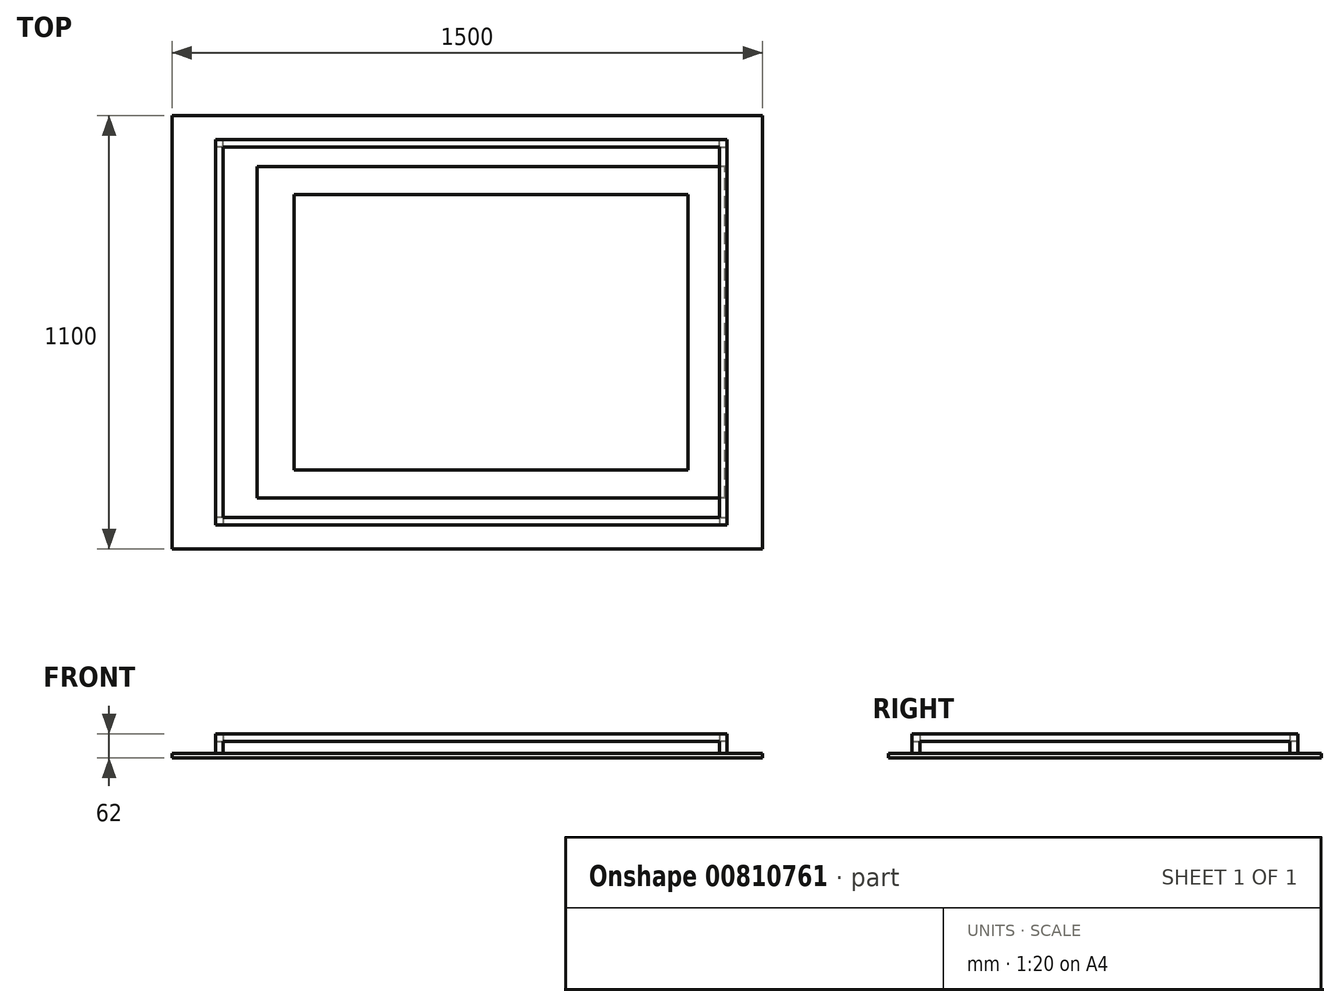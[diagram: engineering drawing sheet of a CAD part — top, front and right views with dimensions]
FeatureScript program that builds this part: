
annotation { "Feature Type Name" : "Feature", "Feature Type Description" : "" }
export const myFeature = defineFeature(function(context is Context, id is Id, definition is map)
    precondition{}
    {
        {
            assignVariable(context, id + "F0", {"name" : "frame_offset", "anyValue" : 40});
        }
        {
            var Q0;
            Q0=qCreatedBy(makeId("Top.planeOp"),FACE);
            var sketch = newSketch(context, id + "F1", { "sketchPlane" : qUnion([Q0])});
            skPoint(sketch, "E0.middle", {"position": v(0, 0) * mm});
            skLineSegment(sketch, "E1.bottom", {"start": v(-640, 480) * mm, "end": v(640, 480) * mm, "construction": true});
            skLineSegment(sketch, "E1.top", {"start": v(-640, -480) * mm, "end": v(640, -480) * mm, "construction": true});
            skLineSegment(sketch, "E1.left", {"start": v(-640, 480) * mm, "end": v(-640, -480) * mm, "construction": true});
            skLineSegment(sketch, "E1.right", {"start": v(640, 480) * mm, "end": v(640, -480) * mm, "construction": true});
            skLineSegment(sketch, "E2.bottom", {"start": v(740, 550) * mm, "end": v(-760, 550) * mm});
            skLineSegment(sketch, "E2.top", {"start": v(740, -550) * mm, "end": v(-760, -550) * mm});
            skLineSegment(sketch, "E2.left", {"start": v(740, 550) * mm, "end": v(740, -550) * mm});
            skLineSegment(sketch, "E2.right", {"start": v(-760, 550) * mm, "end": v(-760, -550) * mm});
            skPoint(sketch, "E2.middle", {"position": v(-10, 0) * mm});
            skLineSegment(sketch, "E3.bottom", {"start": v(-485, 360) * mm, "end": v(585, 360) * mm, "construction": true});
            skLineSegment(sketch, "E3.top", {"start": v(-485, -360) * mm, "end": v(585, -360) * mm, "construction": true});
            skLineSegment(sketch, "E3.left", {"start": v(-485, 360) * mm, "end": v(-485, -360) * mm, "construction": true});
            skLineSegment(sketch, "E3.right", {"start": v(585, 360) * mm, "end": v(585, -360) * mm, "construction": true});
            skPoint(sketch, "E3.middle", {"position": v(50, 0) * mm});
            skSolve(sketch);
        }
        {
            var Q0;
            Q0=qCreatedBy(makeId("Top.planeOp"),FACE);
            var sketch = newSketch(context, id + "F2", { "sketchPlane" : qUnion([Q0])});
            skLineSegment(sketch, "E4.bottom", {"start": v(400, 250) * mm, "end": v(-300, 250) * mm, "construction": true});
            skLineSegment(sketch, "E4.top", {"start": v(400, -250) * mm, "end": v(-300, -250) * mm, "construction": true});
            skLineSegment(sketch, "E4.left", {"start": v(400, 250) * mm, "end": v(400, -250) * mm, "construction": true});
            skLineSegment(sketch, "E4.right", {"start": v(-300, 250) * mm, "end": v(-300, -250) * mm, "construction": true});
            skPoint(sketch, "E4.middle", {"position": v(50, 0) * mm});
            skLineSegment(sketch, "E5.bottom", {"start": v(644.5, -420.5) * mm, "end": v(-544.5, -420.5) * mm, "construction": true});
            skLineSegment(sketch, "E5.top", {"start": v(644.5, 420.5) * mm, "end": v(-544.5, 420.5) * mm, "construction": true});
            skLineSegment(sketch, "E5.left", {"start": v(644.5, -420.5) * mm, "end": v(644.5, 420.5) * mm, "construction": true});
            skLineSegment(sketch, "E5.right", {"start": v(-544.5, -420.5) * mm, "end": v(-544.5, 420.5) * mm, "construction": true});
            skLineSegment(sketch, "E6.bottom", {"start": v(550, 350) * mm, "end": v(-450, 350) * mm, "construction": true});
            skLineSegment(sketch, "E6.top", {"start": v(550, -350) * mm, "end": v(-450, -350) * mm, "construction": true});
            skLineSegment(sketch, "E6.left", {"start": v(550, 350) * mm, "end": v(550, -350) * mm, "construction": true});
            skLineSegment(sketch, "E6.right", {"start": v(-450, 350) * mm, "end": v(-450, -350) * mm, "construction": true});
            skSolve(sketch);
        }
        {
            var Q0;
            Q0=qSketchRegion(id+"F1",true);
            extrude(context, id + "F3", {"entities" : qUnion([Q0]), "oppositeDirection" : true, "depth" : 12 * mm});
        }
        {
            var Q0;
            Q0=qCreatedBy(makeId("Top.planeOp"),FACE);
            cPlane(context, id + "F4", {"entities" : qUnion([Q0]), "cplaneType" : CPlaneType.OFFSET, "offset" : (getVariable(context, 'frame_offset')) * mm, "width" : 150 * mm, "height" : 150 * mm});
        }
        {
            var Q0;
            Q0=qCreatedBy(id+"F4.planeOp",FACE);
            var sketch = newSketch(context, id + "F5", { "sketchPlane" : qUnion([Q0])});
            skLineSegment(sketch, "E7.bottom", {"start": v(-650, 490) * mm, "end": v(650, 490) * mm});
            skLineSegment(sketch, "E7.top", {"start": v(-650, -490) * mm, "end": v(650, -490) * mm});
            skLineSegment(sketch, "E7.left", {"start": v(-650, 490) * mm, "end": v(-650, -490) * mm});
            skLineSegment(sketch, "E7.right", {"start": v(650, 490) * mm, "end": v(650, -490) * mm});
            skLineSegment(sketch, "E8.bottom", {"start": v(-630, 470) * mm, "end": v(630, 470) * mm});
            skLineSegment(sketch, "E8.top", {"start": v(-630, -470) * mm, "end": v(630, -470) * mm});
            skLineSegment(sketch, "E8.left", {"start": v(-630, 470) * mm, "end": v(-630, -470) * mm});
            skLineSegment(sketch, "E8.right", {"start": v(630, 470) * mm, "end": v(630, -470) * mm});
            skSolve(sketch);
        }
        {
            var Q0;
            Q0=qSketchRegion(id+"F5",true);
            extrude(context, id + "F6", {"entities" : qUnion([Q0]), "depth" : 20 * mm, "symmetric" : true});
        }
        {
            var Q0;
            Q0=makeQuery(id+"F6.opExtrude","CAP_FACE",FACE,{"disambiguationData":[OSD([sQuery(id+"F5.wireOp",EDGE,"E7.bottom"),sQuery(id+"F5.wireOp",EDGE,"E7.top"),sQuery(id+"F5.wireOp",EDGE,"E7.left"),sQuery(id+"F5.wireOp",EDGE,"E7.right"),sQuery(id+"F5.wireOp",EDGE,"E8.bottom"),sQuery(id+"F5.wireOp",EDGE,"E8.top"),sQuery(id+"F5.wireOp",EDGE,"E8.left"),sQuery(id+"F5.wireOp",EDGE,"E8.right")])],"isStart":false});
            var sketch = newSketch(context, id + "F7", { "sketchPlane" : qUnion([Q0])});
            skLineSegment(sketch, "E9.bottom", {"start": v(-650, 490) * mm, "end": v(-630, 490) * mm});
            skLineSegment(sketch, "E9.top", {"start": v(-650, 470) * mm, "end": v(-630, 470) * mm});
            skLineSegment(sketch, "E9.left", {"start": v(-650, 490) * mm, "end": v(-650, 470) * mm});
            skLineSegment(sketch, "E9.right", {"start": v(-630, 490) * mm, "end": v(-630, 470) * mm});
            skLineSegment(sketch, "E10.bottom", {"start": v(650, 490) * mm, "end": v(630, 490) * mm});
            skLineSegment(sketch, "E10.top", {"start": v(650, 470) * mm, "end": v(630, 470) * mm});
            skLineSegment(sketch, "E10.left", {"start": v(650, 490) * mm, "end": v(650, 470) * mm});
            skLineSegment(sketch, "E10.right", {"start": v(630, 490) * mm, "end": v(630, 470) * mm});
            skLineSegment(sketch, "E11.bottom", {"start": v(650, -490) * mm, "end": v(630, -490) * mm});
            skLineSegment(sketch, "E11.top", {"start": v(650, -470) * mm, "end": v(630, -470) * mm});
            skLineSegment(sketch, "E11.left", {"start": v(650, -490) * mm, "end": v(650, -470) * mm});
            skLineSegment(sketch, "E11.right", {"start": v(630, -490) * mm, "end": v(630, -470) * mm});
            skLineSegment(sketch, "E12.bottom", {"start": v(-650, -490) * mm, "end": v(-630, -490) * mm});
            skLineSegment(sketch, "E12.top", {"start": v(-650, -470) * mm, "end": v(-630, -470) * mm});
            skLineSegment(sketch, "E12.left", {"start": v(-650, -490) * mm, "end": v(-650, -470) * mm});
            skLineSegment(sketch, "E12.right", {"start": v(-630, -490) * mm, "end": v(-630, -470) * mm});
            skSolve(sketch);
        }
        {
            var Q0;
            Q0=qSketchRegion(id+"F7",true);
            var Q1;
            Q1=makeQuery(id+"F3.opExtrude","SWEPT_BODY",BODY,{"disambiguationData":[OSD([sQuery(id+"F1.wireOp",EDGE,"E2.bottom"),sQuery(id+"F1.wireOp",EDGE,"E2.top"),sQuery(id+"F1.wireOp",EDGE,"E2.left"),sQuery(id+"F1.wireOp",EDGE,"E2.right")])]});
            extrude(context, id + "F8", {"entities" : qUnion([Q0]), "operationType" : NewBodyOperationType.ADD, "endBound" : BoundingType.UP_TO_BODY, "oppositeDirection" : true, "endBoundEntityBody" : qUnion([Q1]), "depth" : 25 * mm});
        }
        {
            var Q0;
            Q0=qSketchRegion(id+"F1",true);
            extrude(context, id + "F9", {"entities" : qUnion([Q0]), "oppositeDirection" : true, "depth" : 12 * mm});
        }
        {
            var Q0;
            Q0=makeQuery(id+"F1.imprint","IMPRINT",FACE,{"disambiguationData":[TD([[makeQuery(id+"F1.imprint","IMPRINT",EDGE,{"derivedFrom":sQuery(id+"F1.wireOp",EDGE,"E2.bottom")}),1.0]])]});
            var sketch = newSketch(context, id + "F10", { "sketchPlane" : qUnion([Q0])});
            skLineSegment(sketch, "E13.0", {"start": v(-544.5, -420.5) * mm, "end": v(-544.5, 420.5) * mm});
            skLineSegment(sketch, "E13.1", {"start": v(644.5, 420.5) * mm, "end": v(-544.5, 420.5) * mm});
            skLineSegment(sketch, "E13.2", {"start": v(644.5, -420.5) * mm, "end": v(-544.5, -420.5) * mm});
            skLineSegment(sketch, "E13.3", {"start": v(644.5, -420.5) * mm, "end": v(644.5, 420.5) * mm});
            skSolve(sketch);
        }
        {
            var Q0;
            Q0=qSketchRegion(id+"F10",true);
            extrude(context, id + "F11", {"entities" : qUnion([Q0]), "depth" : .2 * mm});
        }
        {
            var Q0;
            Q0=makeQuery(id+"F1.imprint","IMPRINT",FACE,{"disambiguationData":[TD([[makeQuery(id+"F1.imprint","IMPRINT",EDGE,{"derivedFrom":sQuery(id+"F1.wireOp",EDGE,"E2.bottom")}),1.0]])]});
            var sketch = newSketch(context, id + "F12", { "sketchPlane" : qUnion([Q0])});
            skLineSegment(sketch, "E14.0", {"start": v(-450, 350) * mm, "end": v(-450, -350) * mm});
            skLineSegment(sketch, "E14.1", {"start": v(550, 350) * mm, "end": v(-450, 350) * mm});
            skLineSegment(sketch, "E14.2", {"start": v(550, 350) * mm, "end": v(550, -350) * mm});
            skLineSegment(sketch, "E14.3", {"start": v(550, -350) * mm, "end": v(-450, -350) * mm});
            skSolve(sketch);
        }
        {
            var Q0;
            Q0=qSketchRegion(id+"F12",true);
            var Q1;
            Q1=qConstructionFilter(qBodyType(qCreatedBy(id+"F12",EDGE),BodyType.WIRE),ConstructionObject.NO);
            extrude(context, id + "F13", {"entities" : qUnion([Q0]), "surfaceEntities" : qUnion([Q1]), "depth" : .2 * mm});
        }
    });
